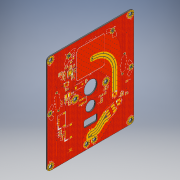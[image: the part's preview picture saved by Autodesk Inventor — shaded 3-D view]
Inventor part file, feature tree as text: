
AUTODESK INVENTOR PART (.ipt)
format: ipt  version: 2018 (Build 220112000, 112)  size: 1,262,080 bytes
history: native  units: mm
features: sketch x13, hole x9, other x4, extrude x2
ambient origin geometry x8: Origin, YZ Plane, XZ Plane, XY Plane, X Axis, Y Axis, Z Axis, Center Point
bodies: Solid1 (feature_tree)
feature tree (28):
  extrude  "Extrusion1"  Depth=79.0mm
  extrude  "Extrusion2"  Depth=1.0mm
  other  "Decal4"
  other  "Decal5"
  hole  "Hole15"  [1 undecoded]
  hole  "Hole16"  [1 undecoded]
  hole  "Hole17"  [1 undecoded]
  hole  "Hole18"  [1 undecoded]
  hole  "Hole19"  [1 undecoded]
  hole  "Hole20"  [1 undecoded]
  hole  "Hole21"  [1 undecoded]
  hole  "Hole22"  [1 undecoded]
  hole  "Hole23"  [1 undecoded]
  sketch  "Sketch1"  dims[d2=28.0mm d3=79.0mm]
  sketch  "Sketch3"  dims[d6=1.0mm d7=0.0mm d15=2.5mm]
  sketch  "Sketch17"  dims[d16=12.0mm d17=14.85mm]
  sketch  "Sketch18"  dims[d18=9.0mm d21=10.0mm d22=0.0mm]
  other  "Image7"
  sketch  "Sketch19"  dims[d84=24.0mm d85=12.0mm]
  sketch  "Sketch20"  dims[d86=6.0mm d87=1.0mm]
  sketch  "Sketch21"  dims[d117=3.0mm d118=90.0mm]
  sketch  "Sketch22"  dims[d119=84.0mm d120=73.0mm]
  sketch  "Sketch23"  dims[d245=3.3mm d246=6.0mm d247=4.0mm d248=2.0mm d249=90.0deg d250=8.0mm d251=20.594885mm]
  sketch  "Sketch24"  dims[d252=3.0mm d253=6.0mm d254=4.0mm d255=2.0mm d256=90.0deg d257=8.0mm d258=20.594885mm]
  sketch  "Sketch25"  dims[d259=2.2mm d260=6.0mm d261=4.0mm d262=2.0mm d263=90.0deg d264=8.0mm d265=20.594885mm]
  sketch  "Sketch26"  dims[d266=1.0mm d267=6.0mm d268=4.0mm d269=2.0mm d270=90.0deg d271=8.0mm d272=20.594885mm]
  sketch  "Sketch27"  dims[d273=0.95mm d274=6.0mm d275=4.0mm d276=2.0mm d277=90.0deg d278=8.0mm d279=20.594885mm d280=0.7mm d281=6.0mm d282=4.0mm d283=2.0mm d284=90.0deg d285=8.0mm d286=20.594885mm d287=0.45mm d288=6.0mm d289=4.0mm d290=2.0mm d291=90.0deg d292=8.0mm d293=20.594885mm d294=0.35mm d295=6.0mm d296=4.0mm d297=2.0mm d298=90.0deg d299=8.0mm d300=20.594885mm d301=0.3mm d302=6.0mm d303=4.0mm d304=2.0mm d305=90.0deg d306=8.0mm d307=20.594885mm]
  other  "Image8"
note: 9 required parameter values undecoded (feature->parameter linkage not recoverable at this tier; creation-order binding heuristic only, values carry confidence <= 0.55)
